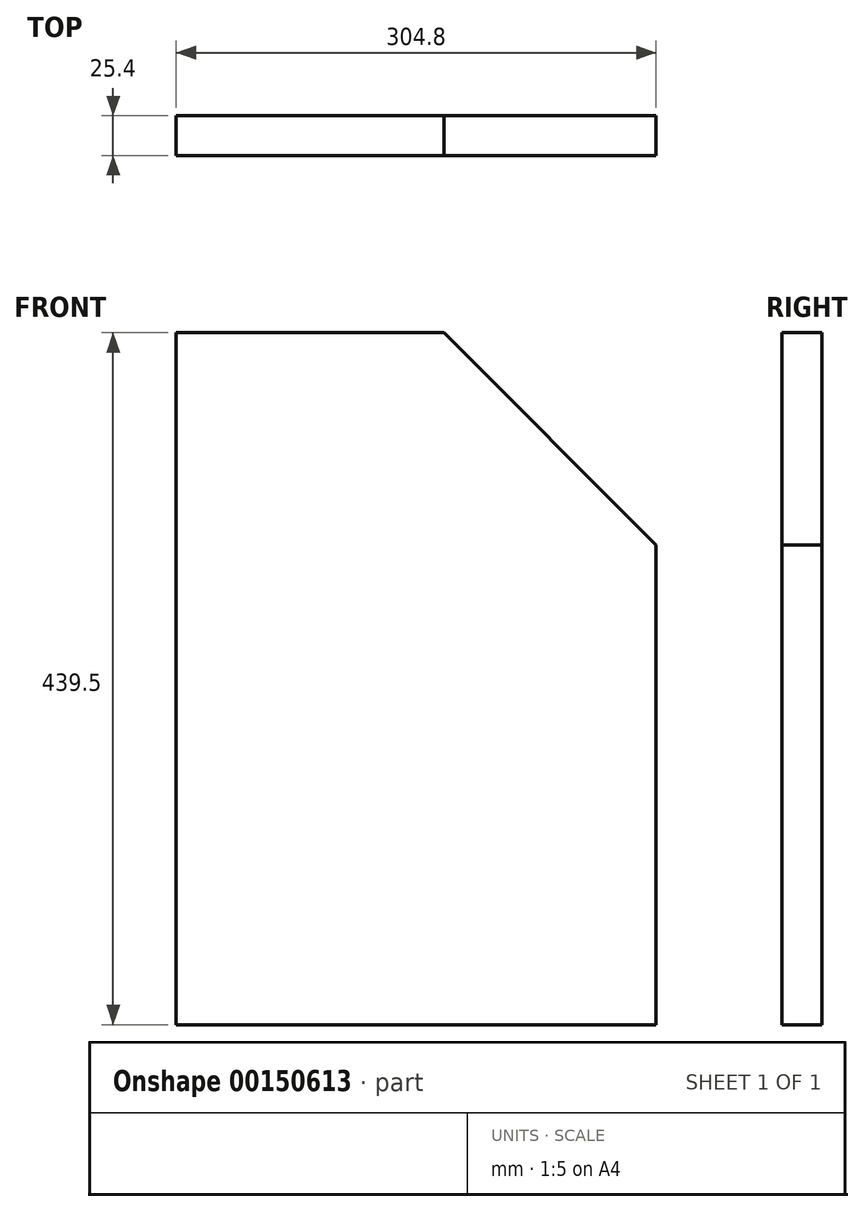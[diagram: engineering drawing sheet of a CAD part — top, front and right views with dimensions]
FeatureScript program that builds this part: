
annotation { "Feature Type Name" : "Feature", "Feature Type Description" : "" }
export const myFeature = defineFeature(function(context is Context, id is Id, definition is map)
    precondition{}
    {
        {
            var Q0;
            Q0=qCreatedBy(makeId("Front.planeOp"),FACE);
            var sketch = newSketch(context, id + "F0", { "sketchPlane" : qUnion([Q0])});
            skLineSegment(sketch, "E0", {"start": v(152.74, -195.4) * mm, "end": v(-152.06, -195.4) * mm});
            skLineSegment(sketch, "E1", {"start": v(-152.06, -195.4) * mm, "end": v(-152.06, 244.1) * mm});
            skLineSegment(sketch, "E2", {"start": v(-152.06, 244.1) * mm, "end": v(18.04, 244.1) * mm});
            skLineSegment(sketch, "E3", {"start": v(18.04, 244.1) * mm, "end": v(152.74, 109.4) * mm});
            skLineSegment(sketch, "E4", {"start": v(152.74, 109.4) * mm, "end": v(152.74, -195.4) * mm});
            skLineSegment(sketch, "E5", {"start": v(152.74, 109.4) * mm, "end": v(-152.06, 109.4) * mm});
            skSolve(sketch);
        }
        {
            var Q0;
            Q0 = qSketchRegion(id + "F0", true);
            extrude(context, id + "F1", {"entities" : qUnion([Q0]), "depth" : 25.4 * mm});
        }
    });
